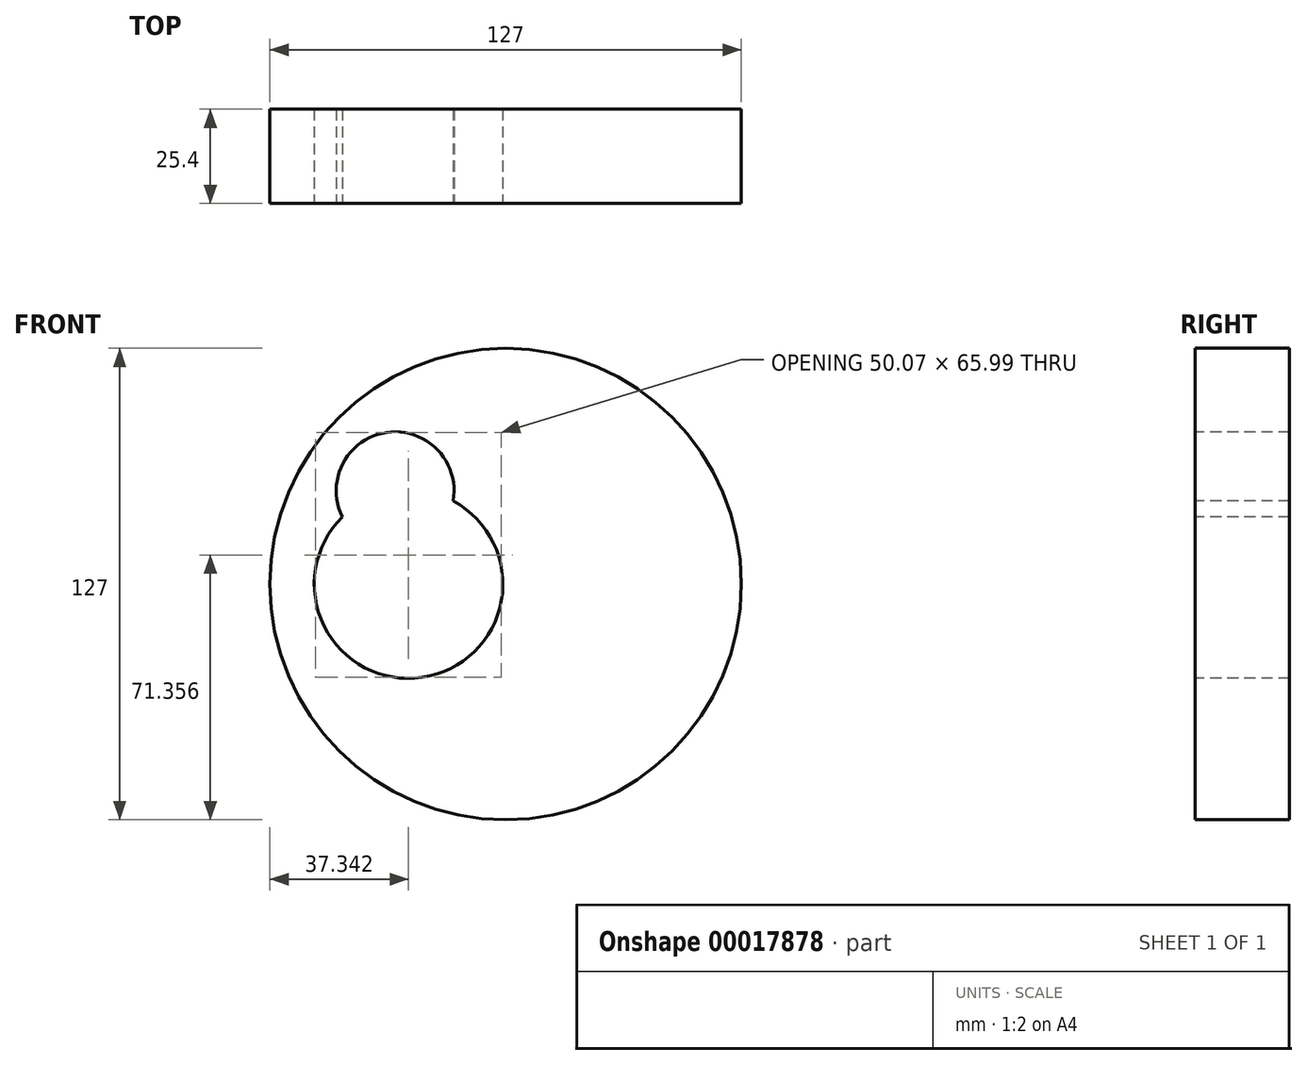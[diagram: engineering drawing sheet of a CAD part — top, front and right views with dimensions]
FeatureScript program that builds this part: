
annotation { "Feature Type Name" : "Feature", "Feature Type Description" : "" }
export const myFeature = defineFeature(function(context is Context, id is Id, definition is map)
    precondition{}
    {
        {
            var Q0;
            Q0=qCreatedBy(makeId("Front.planeOp"),FACE);
            var sketch = newSketch(context, id + "F0", { "sketchPlane" : qUnion([Q0])});
            skCircle(sketch, "E0", {"center": v(0, 0) * mm, "radius": 63.5 * mm});
            skSolve(sketch);
        }
        {
            var Q0;
            Q0 = qSketchRegion(id + "F0", true);
            extrude(context, id + "F1", {"entities" : qUnion([Q0]), "depth" : 25.4 * mm});
        }
        {
            var Q0;
            Q0=makeQuery(id+"F1.opExtrude","CAP_FACE",FACE,{"disambiguationData":[OSD([sQuery(id+"F0.wireOp",EDGE,"E0")])],"isStart":false});
            var sketch = newSketch(context, id + "F2", { "sketchPlane" : qUnion([Q0])});
            skArc(sketch, "E1", {"start": v(-43.98, 18.08) * mm, "mid": v(-22.52, -25.14) * mm, "end": v(-14.13, 22.38) * mm});
            skArc(sketch, "E2", {"start": v(-14.13, 22.38) * mm, "mid": v(-32.02, 40.85) * mm, "end": v(-43.98, 18.08) * mm});
            skSolve(sketch);
        }
        {
            var Q0;
            Q0 = qSketchRegion(id + "F2", true);
            extrude(context, id + "F3", {"entities" : qUnion([Q0]), "operationType" : NewBodyOperationType.REMOVE, "oppositeDirection" : true, "depth" : 25.4 * mm});
        }
    });
